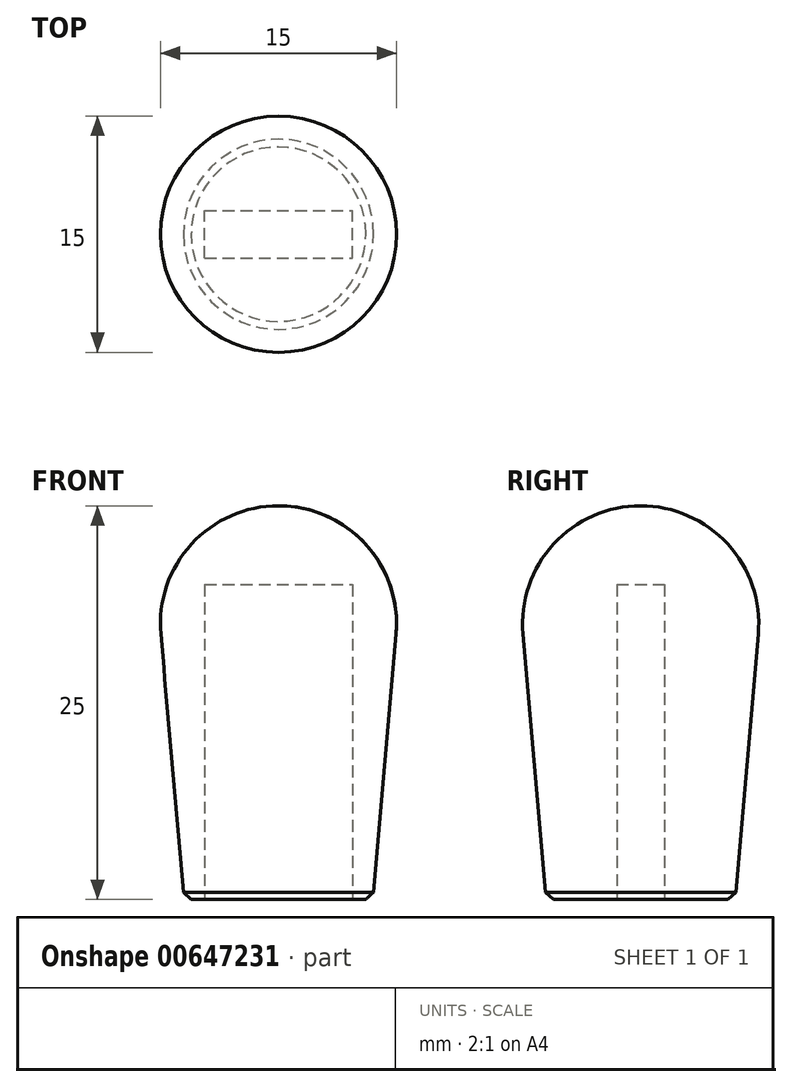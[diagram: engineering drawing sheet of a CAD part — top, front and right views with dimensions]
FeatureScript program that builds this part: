
annotation { "Feature Type Name" : "Feature", "Feature Type Description" : "" }
export const myFeature = defineFeature(function(context is Context, id is Id, definition is map)
    precondition{}
    {
        {
            var Q0;
            Q0=qCreatedBy(makeId("Front.planeOp"),FACE);
            var sketch = newSketch(context, id + "F0", { "sketchPlane" : qUnion([Q0])});
            skLineSegment(sketch, "E0", {"start": v(0, 0) * mm, "end": v(0, 27.93) * mm, "construction": true});
            skArc(sketch, "E1", {"start": v(0, 25) * mm, "mid": v(-5.53, 22.57) * mm, "end": v(-7.47, 16.85) * mm});
            skLineSegment(sketch, "E2", {"start": v(-7.47, 16.85) * mm, "end": v(-6, 0) * mm});
            skLineSegment(sketch, "E3", {"start": v(-6, 0) * mm, "end": v(0, 0) * mm});
            skLineSegment(sketch, "E4", {"start": v(0, 25) * mm, "end": v(0, 0) * mm});
            skSolve(sketch);
        }
        {
            var Q0;
            Q0=makeQuery(id+"F0.imprint","IMPRINT",FACE,{"disambiguationData":[TD([[makeQuery(id+"F0.imprint","IMPRINT",EDGE,{"derivedFrom":sQuery(id+"F0.wireOp",EDGE,"E1")}),1.0]])]});
            var Q1;
            Q1=sQuery(id+"F0.wireOp",EDGE,"E0");
            revolve(context, id + "F1", {"entities" : qUnion([Q0]), "axis" : qUnion([Q1]), "revolveType" : RevolveType.FULL});
        }
        {
            var Q0;
            Q0=makeQuery(id+"F1.opRevolve","SWEPT_FACE",FACE,{"disambiguationData":[OSD([sQuery(id+"F0.wireOp",EDGE,"E3")])]});
            var sketch = newSketch(context, id + "F2", { "sketchPlane" : qUnion([Q0])});
            skLineSegment(sketch, "E5.bottom", {"start": v(-4.7, 1.51) * mm, "end": v(4.7, 1.51) * mm});
            skLineSegment(sketch, "E5.top", {"start": v(-4.7, -1.51) * mm, "end": v(4.7, -1.51) * mm});
            skLineSegment(sketch, "E5.left", {"start": v(-4.7, 1.51) * mm, "end": v(-4.7, -1.51) * mm});
            skLineSegment(sketch, "E5.right", {"start": v(4.7, 1.51) * mm, "end": v(4.7, -1.51) * mm});
            skPoint(sketch, "E6", {"position": v(-4.7, 0) * mm});
            skPoint(sketch, "E7", {"position": v(0, 1.51) * mm});
            skSolve(sketch);
        }
        {
            var Q0;
            Q0=makeQuery(id+"F2.imprint","IMPRINT",FACE,{"disambiguationData":[TD([[makeQuery(id+"F2.imprint","IMPRINT",EDGE,{"derivedFrom":sQuery(id+"F2.wireOp",EDGE,"E5.bottom")}),-1.0]])]});
            extrude(context, id + "F3", {"entities" : qUnion([Q0]), "operationType" : NewBodyOperationType.REMOVE, "oppositeDirection" : true, "depth" : 20 * mm, "offsetDistance" : 25 * mm});
        }
        {
            var Q0;
            Q0=makeQuery(id+"F1.opRevolve","SWEPT_EDGE",EDGE,{"disambiguationData":[OSD([sQuery(id+"F0.wireOp",EDGE,"E2"),sQuery(id+"F0.wireOp",EDGE,"E3")])]});
            chamfer(context, id + "F4", {"entities" : qUnion([Q0]), "width" : 0.5 * mm, "tangentPropagation" : true});
        }
    });
